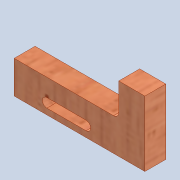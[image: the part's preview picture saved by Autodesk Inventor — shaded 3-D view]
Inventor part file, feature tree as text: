
AUTODESK INVENTOR PART (.ipt)
format: ipt  version: 2020 (Build 240168000, 168)  size: 260,608 bytes
history: native  units: mm
features: extrude x3, sketch x3, fillet x1
ambient origin geometry x8: Origin, YZ Plane, XZ Plane, XY Plane, X Axis, Y Axis, Z Axis, Center Point
bodies: Solid1 (feature_tree)
feature tree (7):
  extrude  "Extrusion1"  Depth=25.0mm
  extrude  "Extrusion5"  Depth=3.5mm
  extrude  "Extrusion6"  Depth=2.0mm
  fillet  "Fillet1"  Radius=20.0mm
  sketch  "Sketch1"  dims[d0=50.0mm d1=25.0mm]
  sketch  "Sketch5"  dims[d2=8.0mm d3=0.0mm d29=3.5mm]
  sketch  "Sketch6"  dims[d30=4.0mm d31=4.0mm d32=20.0mm d33=15.0mm d34=15.0mm d35=0.0mm d36=10.0mm d37=10.0mm d38=0.0mm d39=2.0mm]
